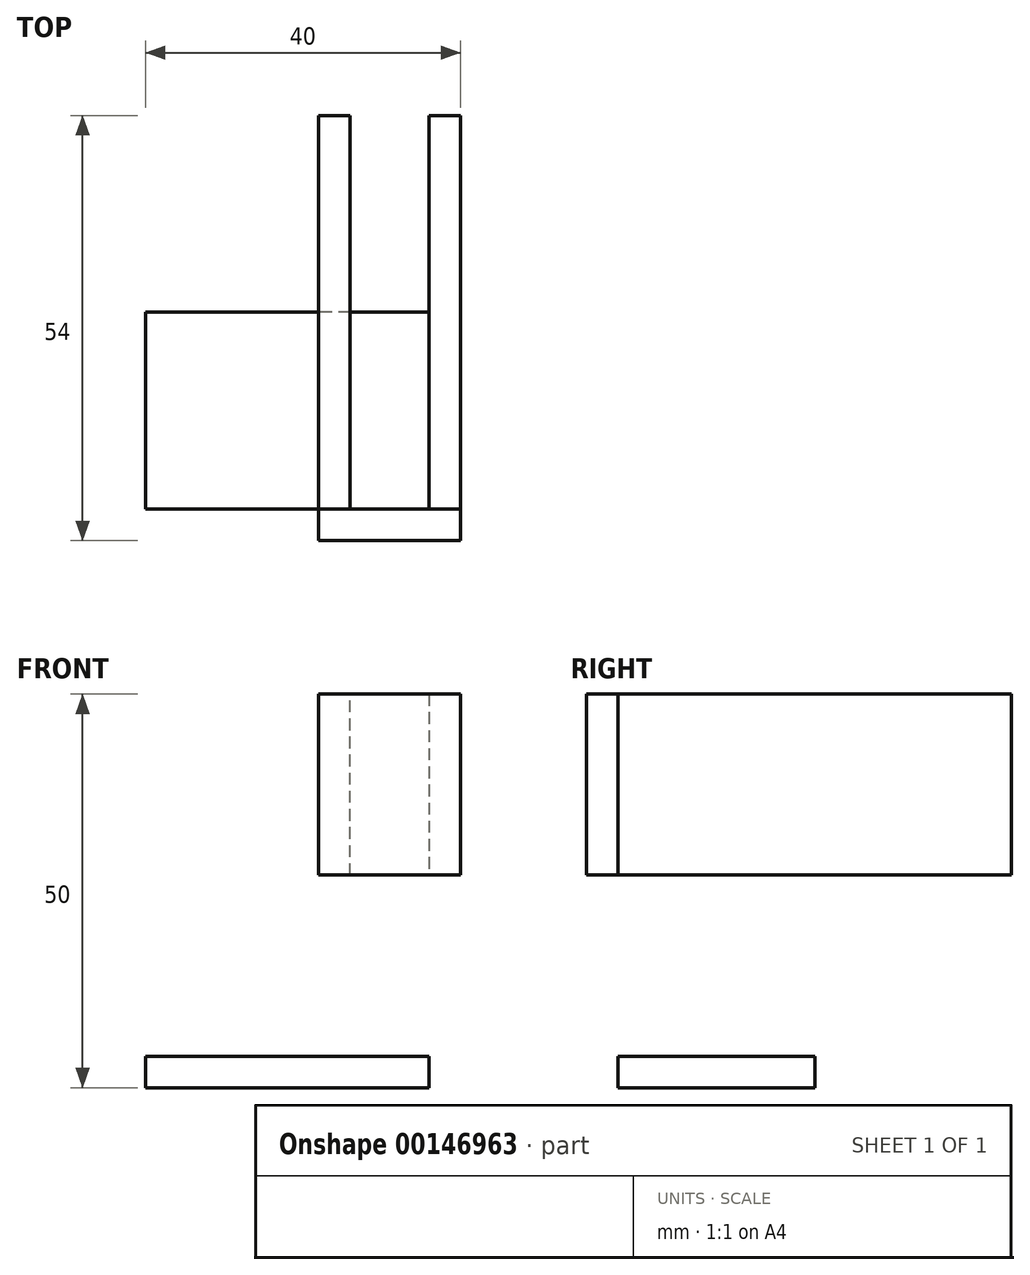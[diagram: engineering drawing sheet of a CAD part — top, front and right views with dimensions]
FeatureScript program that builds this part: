
annotation { "Feature Type Name" : "Feature", "Feature Type Description" : "" }
export const myFeature = defineFeature(function(context is Context, id is Id, definition is map)
    precondition{}
    {
        {
            var Q0;
            Q0=qCreatedBy(makeId("Front.planeOp"),FACE);
            var sketch = newSketch(context, id + "F0", { "sketchPlane" : qUnion([Q0])});
            skLineSegment(sketch, "E0.bottom", {"start": v(0, 0) * mm, "end": v(18, 0) * mm});
            skLineSegment(sketch, "E0.top", {"start": v(0, 23) * mm, "end": v(18, 23) * mm});
            skLineSegment(sketch, "E0.left", {"start": v(0, 0) * mm, "end": v(0, 23) * mm});
            skLineSegment(sketch, "E0.right", {"start": v(18, 0) * mm, "end": v(18, 23) * mm});
            skLineSegment(sketch, "E1", {"start": v(4, 0) * mm, "end": v(4, 23) * mm});
            skLineSegment(sketch, "E2", {"start": v(14, 23) * mm, "end": v(14, 0) * mm});
            skLineSegment(sketch, "E3.bottom", {"start": v(18, 0) * mm, "end": v(14, 0) * mm});
            skLineSegment(sketch, "E3.top", {"start": v(18, -27) * mm, "end": v(14, -27) * mm});
            skLineSegment(sketch, "E3.left", {"start": v(18, 0) * mm, "end": v(18, -27) * mm});
            skLineSegment(sketch, "E3.right", {"start": v(14, 0) * mm, "end": v(14, -27) * mm});
            skLineSegment(sketch, "E4.bottom", {"start": v(14, -27) * mm, "end": v(-22, -27) * mm});
            skLineSegment(sketch, "E4.top", {"start": v(14, -23) * mm, "end": v(-22, -23) * mm});
            skLineSegment(sketch, "E4.left", {"start": v(14, -27) * mm, "end": v(14, -23) * mm});
            skLineSegment(sketch, "E4.right", {"start": v(-22, -27) * mm, "end": v(-22, -23) * mm});
            skSolve(sketch);
        }
        {
            var Q0;
            {var subQ0=sQuery(id+"F0.wireOp",EDGE,"E0.left");Q0=makeQuery(id+"F0.imprint","IMPRINT",FACE,{"disambiguationData":[TD([[makeQuery(id+"F0.imprint","IMPRINT",EDGE,{"derivedFrom":subQ0}),-1.0]])]});}
            var Q1;
            {var subQ0=sQuery(id+"F0.wireOp",EDGE,"E0.right");Q1=makeQuery(id+"F0.imprint","IMPRINT",FACE,{"disambiguationData":[TD([[makeQuery(id+"F0.imprint","IMPRINT",EDGE,{"derivedFrom":subQ0}),1.0]])]});}
            extrude(context, id + "F1", {"entities" : qUnion([Q0, Q1]), "oppositeDirection" : true, "depth" : 50 * mm});
        }
        {
            var Q0;
            Q0=makeQuery(id+"F0.imprint","IMPRINT",FACE,{"disambiguationData":[TD([[makeQuery(id+"F0.imprint","IMPRINT",EDGE,{"derivedFrom":sQuery(id+"F0.wireOp",EDGE,"E4.bottom")}),-1.0]])]});
            var Q1;
            Q1=makeQuery(id+"F0.imprint","IMPRINT",FACE,{"disambiguationData":[TD([[makeQuery(id+"F0.imprint","IMPRINT",EDGE,{"derivedFrom":sQuery(id+"F0.wireOp",EDGE,"E3.bottom")}),1.0]])]});
            extrude(context, id + "F2", {"entities" : qUnion([Q0, Q1]), "operationType" : NewBodyOperationType.ADD, "oppositeDirection" : true, "depth" : 25 * mm});
        }
        {
            var Q0;
            {var subQ2=sQuery(id+"F0.wireOp",EDGE,"E1");Q0=makeQuery(id+"F0.imprint","IMPRINT",FACE,{"disambiguationData":[TD([[makeQuery(id+"F0.imprint","IMPRINT",EDGE,{"derivedFrom":subQ2}),-1.0]])]});}
            var Q1;
            {var subQ0=sQuery(id+"F0.wireOp",EDGE,"E0.left");Q1=makeQuery(id+"F0.imprint","IMPRINT",FACE,{"disambiguationData":[TD([[makeQuery(id+"F0.imprint","IMPRINT",EDGE,{"derivedFrom":subQ0}),-1.0]])]});}
            var Q2;
            {var subQ0=sQuery(id+"F0.wireOp",EDGE,"E0.right");Q2=makeQuery(id+"F0.imprint","IMPRINT",FACE,{"disambiguationData":[TD([[makeQuery(id+"F0.imprint","IMPRINT",EDGE,{"derivedFrom":subQ0}),1.0]])]});}
            extrude(context, id + "F3", {"entities" : qUnion([Q0, Q1, Q2]), "depth" : 4 * mm});
        }
    });
